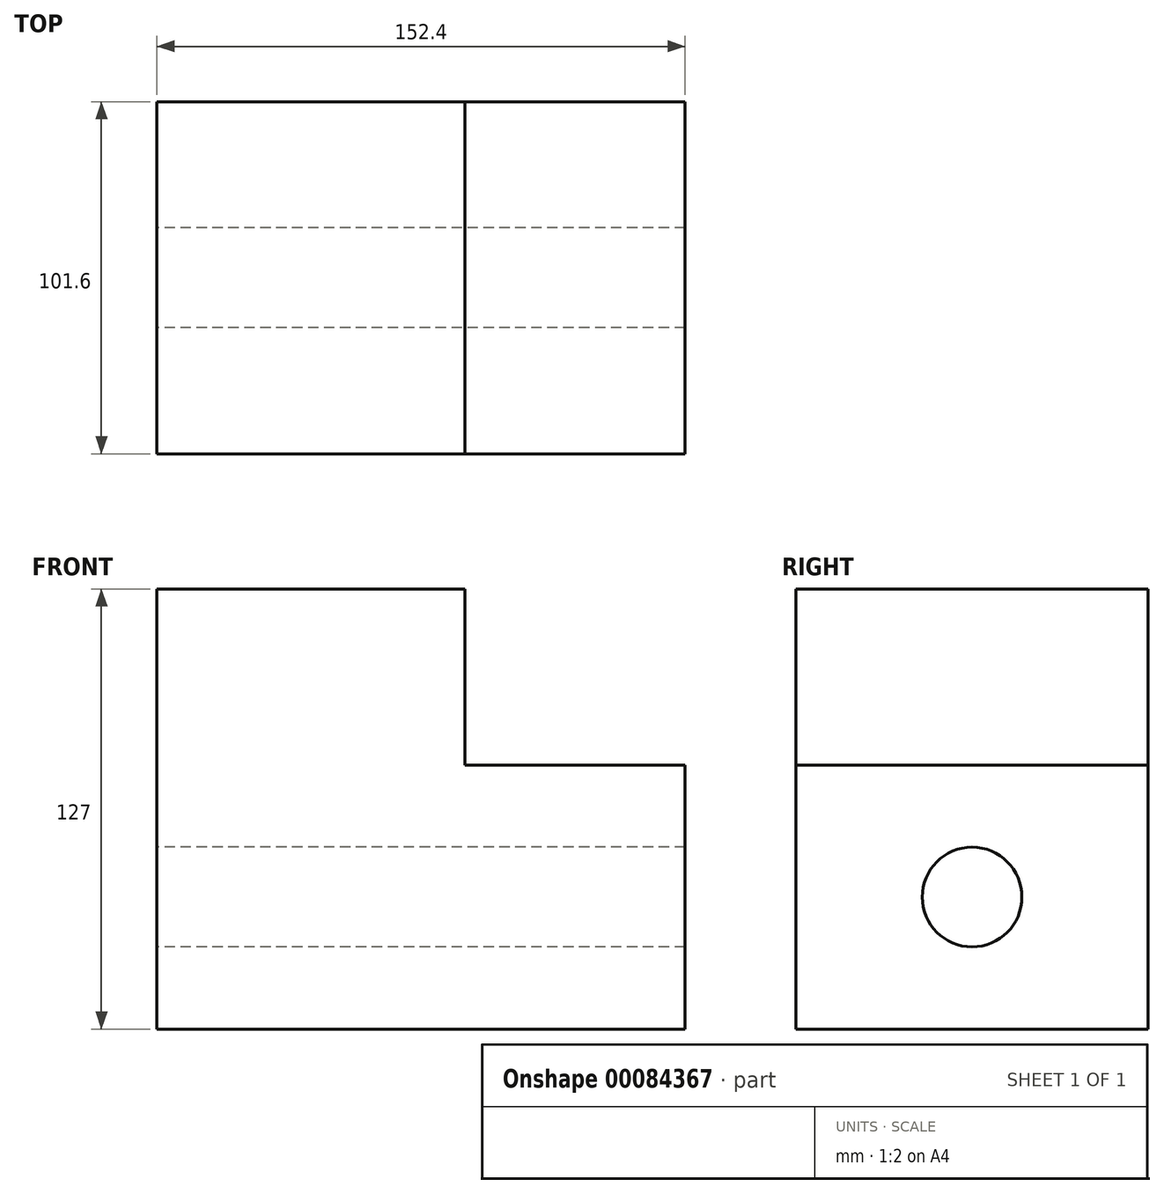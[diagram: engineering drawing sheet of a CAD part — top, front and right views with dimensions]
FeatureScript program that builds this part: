
annotation { "Feature Type Name" : "Feature", "Feature Type Description" : "" }
export const myFeature = defineFeature(function(context is Context, id is Id, definition is map)
    precondition{}
    {
        {
            var Q0;
            Q0=qCreatedBy(makeId("Top.planeOp"),FACE);
            var sketch = newSketch(context, id + "F0", { "sketchPlane" : qUnion([Q0])});
            skLineSegment(sketch, "E0.bottom", {"start": v(-59.68, 54.97) * mm, "end": v(92.72, 54.97) * mm});
            skLineSegment(sketch, "E0.top", {"start": v(-59.68, -46.63) * mm, "end": v(92.72, -46.63) * mm});
            skLineSegment(sketch, "E0.left", {"start": v(-59.68, 54.97) * mm, "end": v(-59.68, -46.63) * mm});
            skLineSegment(sketch, "E0.right", {"start": v(92.72, 54.97) * mm, "end": v(92.72, -46.63) * mm});
            skSolve(sketch);
        }
        {
            var Q0;
            Q0=makeQuery(id+"F0.imprint","IMPRINT",FACE,{"disambiguationData":[TD([[makeQuery(id+"F0.imprint","IMPRINT",EDGE,{"derivedFrom":sQuery(id+"F0.wireOp",EDGE,"E0.bottom")}),-1.0]])]});
            extrude(context, id + "F1", {"entities" : qUnion([Q0]), "depth" : 127 * mm});
        }
        {
            var Q0;
            Q0=makeQuery(id+"F1.opExtrude","SWEPT_FACE",FACE,{"disambiguationData":[OSD([sQuery(id+"F0.wireOp",EDGE,"E0.top")])]});
            var sketch = newSketch(context, id + "F2", { "sketchPlane" : qUnion([Q0])});
            skLineSegment(sketch, "E1.bottom", {"start": v(29.22, 127) * mm, "end": v(92.72, 127) * mm});
            skLineSegment(sketch, "E1.top", {"start": v(29.22, 76.2) * mm, "end": v(92.72, 76.2) * mm});
            skLineSegment(sketch, "E1.left", {"start": v(29.22, 127) * mm, "end": v(29.22, 76.2) * mm});
            skLineSegment(sketch, "E1.right", {"start": v(92.72, 127) * mm, "end": v(92.72, 76.2) * mm});
            skSolve(sketch);
        }
        {
            var Q0;
            Q0=makeQuery(id+"F2.imprint","IMPRINT",FACE,{"disambiguationData":[TD([[makeQuery(id+"F2.imprint","IMPRINT",EDGE,{"derivedFrom":sQuery(id+"F2.wireOp",EDGE,"E1.bottom")}),-1.0]])]});
            extrude(context, id + "F3", {"entities" : qUnion([Q0]), "operationType" : NewBodyOperationType.REMOVE, "oppositeDirection" : true, "depth" : 101.6 * mm});
        }
        {
            var Q0;
            Q0=makeQuery(id+"F1.opExtrude","SWEPT_FACE",FACE,{"disambiguationData":[OSD([sQuery(id+"F0.wireOp",EDGE,"E0.left")])]});
            var sketch = newSketch(context, id + "F4", { "sketchPlane" : qUnion([Q0])});
            skSolve(sketch);
        }
        {
            var Q0;
            {var subQ0=sQuery(id+"F0.wireOp",EDGE,"E0.left");Q0=makeQuery(id+"F4.imprint","IMPRINT",FACE,{"disambiguationData":[TD([[makeQuery(id+"F4.imprint","IMPRINT",EDGE,{"derivedFrom":makeQuery(id+"F1.opExtrude","CAP_EDGE",EDGE,{"disambiguationData":[OSD([subQ0])],"isStart":true})}),1.0]])]});}
            var sketch = newSketch(context, id + "F5", { "sketchPlane" : qUnion([Q0])});
            skCircle(sketch, "E2", {"center": v(-4.17, 38.1) * mm, "radius": 14.38 * mm});
            skSolve(sketch);
        }
        {
            var Q0;
            Q0 = qSketchRegion(id + "F5", true);
            extrude(context, id + "F6", {"entities" : qUnion([Q0]), "operationType" : NewBodyOperationType.REMOVE, "oppositeDirection" : true, "depth" : 152.4 * mm});
        }
    });
